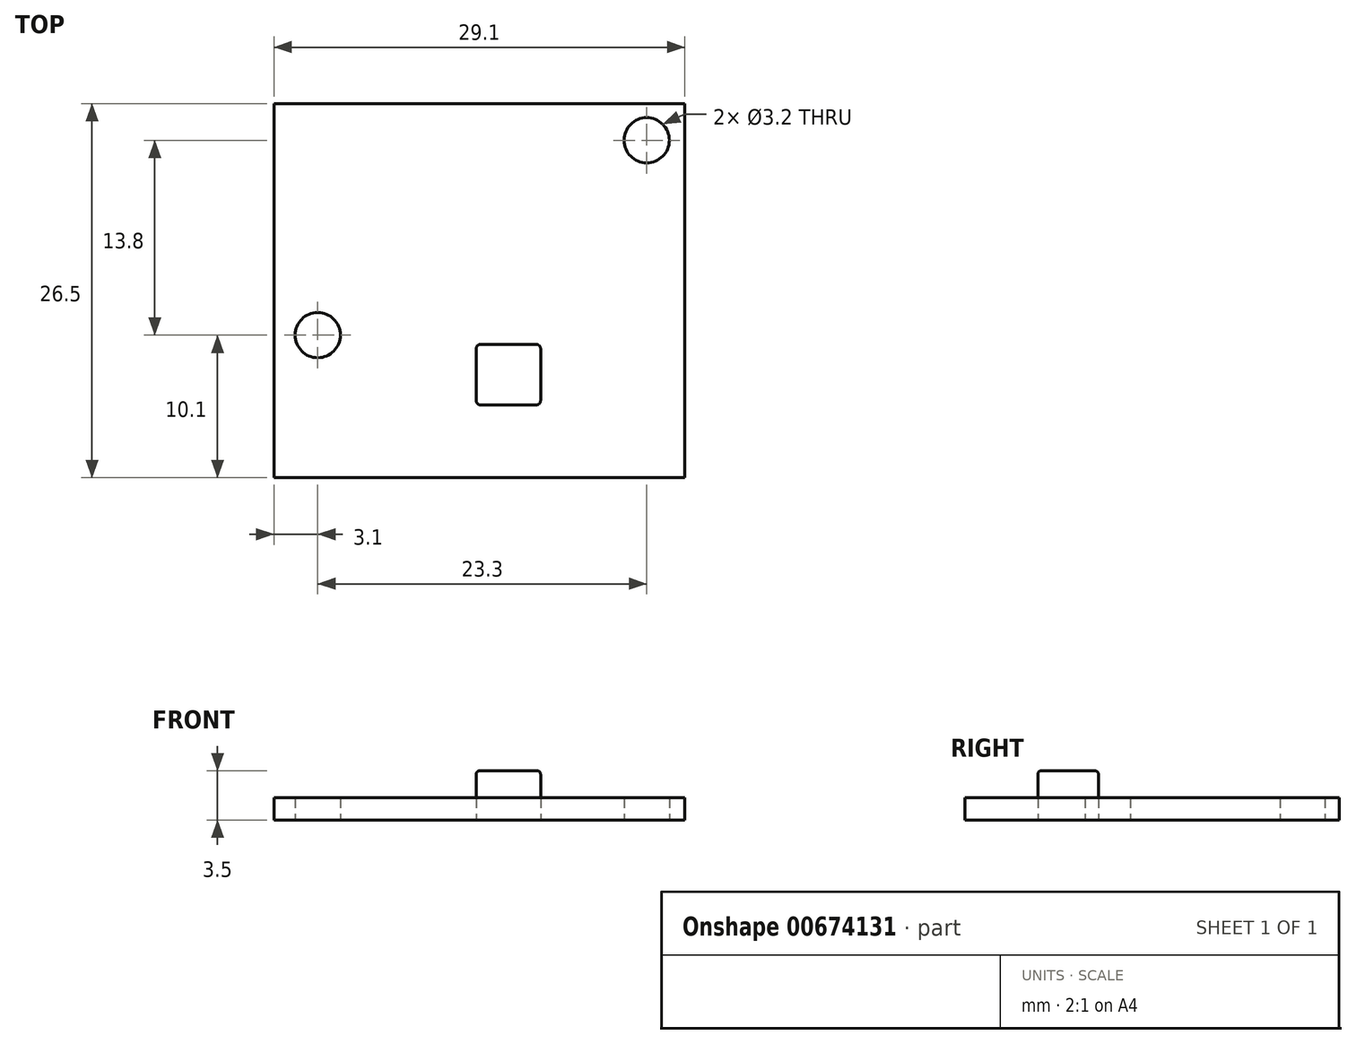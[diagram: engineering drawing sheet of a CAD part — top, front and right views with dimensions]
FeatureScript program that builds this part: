
annotation { "Feature Type Name" : "Feature", "Feature Type Description" : "" }
export const myFeature = defineFeature(function(context is Context, id is Id, definition is map)
    precondition{}
    {
        {
            var Q0;
            Q0=qCreatedBy(makeId("Top.planeOp"),FACE);
            var sketch = newSketch(context, id + "F0", { "sketchPlane" : qUnion([Q0])});
            skLineSegment(sketch, "E0.bottom", {"start": v(14.55, 13.25) * mm, "end": v(-14.55, 13.25) * mm});
            skLineSegment(sketch, "E0.top", {"start": v(14.55, -13.25) * mm, "end": v(-14.55, -13.25) * mm});
            skLineSegment(sketch, "E0.left", {"start": v(14.55, 13.25) * mm, "end": v(14.55, -13.25) * mm});
            skLineSegment(sketch, "E0.right", {"start": v(-14.55, 13.25) * mm, "end": v(-14.55, -13.25) * mm});
            skPoint(sketch, "E0.middle", {"position": v(0, 0) * mm});
            skCircle(sketch, "E1", {"center": v(-11.45, -3.15) * mm, "radius": 1.6 * mm});
            skCircle(sketch, "E2", {"center": v(11.85, 10.65) * mm, "radius": 1.6 * mm});
            skLineSegment(sketch, "E3.bottom", {"start": v(4.03, -8.1) * mm, "end": v(0.07, -8.1) * mm});
            skLineSegment(sketch, "E3.top", {"start": v(4.03, -3.8) * mm, "end": v(0.07, -3.8) * mm});
            skLineSegment(sketch, "E3.left", {"start": v(4.33, -7.8) * mm, "end": v(4.33, -4.1) * mm});
            skLineSegment(sketch, "E3.right", {"start": v(-0.23, -7.8) * mm, "end": v(-0.23, -4.1) * mm});
            skPoint(sketch, "E3.middle", {"position": v(2.05, -5.95) * mm});
            skPoint(sketch, "E4.visualSharp", {"position": v(-0.23, -3.8) * mm});
            skArc(sketch, "E4.filletArc", {"start": v(0.07, -3.8) * mm, "mid": v(-0.14, -3.9) * mm, "end": v(-0.23, -4.1) * mm});
            skPoint(sketch, "E5.visualSharp", {"position": v(4.33, -3.8) * mm});
            skArc(sketch, "E5.filletArc", {"start": v(4.33, -4.1) * mm, "mid": v(4.24, -3.9) * mm, "end": v(4.03, -3.8) * mm});
            skPoint(sketch, "E6.visualSharp", {"position": v(4.33, -8.1) * mm});
            skArc(sketch, "E6.filletArc", {"start": v(4.03, -8.1) * mm, "mid": v(4.24, -8) * mm, "end": v(4.33, -7.8) * mm});
            skPoint(sketch, "E7.visualSharp", {"position": v(-0.23, -8.1) * mm});
            skArc(sketch, "E7.filletArc", {"start": v(-0.23, -7.8) * mm, "mid": v(-0.14, -8) * mm, "end": v(0.07, -8.1) * mm});
            skSolve(sketch);
        }
        {
            var Q0;
            Q0=makeQuery(id+"F0.imprint","IMPRINT",FACE,{"disambiguationData":[TD([[makeQuery(id+"F0.imprint","IMPRINT",EDGE,{"derivedFrom":sQuery(id+"F0.wireOp",EDGE,"E0.bottom")}),1.0]])]});
            var Q1;
            Q1=makeQuery(id+"F0.imprint","IMPRINT",FACE,{"disambiguationData":[TD([[makeQuery(id+"F0.imprint","IMPRINT",EDGE,{"derivedFrom":sQuery(id+"F0.wireOp",EDGE,"E3.bottom")}),-1.0]])]});
            extrude(context, id + "F1", {"entities" : qUnion([Q0, Q1]), "depth" : 1.6 * mm, "offsetDistance" : 25 * mm});
        }
        {
            var Q0;
            Q0=makeQuery(id+"F0.imprint","IMPRINT",FACE,{"disambiguationData":[TD([[makeQuery(id+"F0.imprint","IMPRINT",EDGE,{"derivedFrom":sQuery(id+"F0.wireOp",EDGE,"E3.bottom")}),-1.0]])]});
            extrude(context, id + "F2", {"entities" : qUnion([Q0]), "depth" : 3.5 * mm, "offsetDistance" : 25 * mm});
        }
        {
            var Q0;
            Q0=makeQuery(id+"F2.opExtrude","CAP_FACE",FACE,{"disambiguationData":[OSD([sQuery(id+"F0.wireOp",EDGE,"E3.bottom"),sQuery(id+"F0.wireOp",EDGE,"E3.top"),sQuery(id+"F0.wireOp",EDGE,"E3.left"),sQuery(id+"F0.wireOp",EDGE,"E3.right")])],"isStart":false});
            fillet(context, id + "F3", {"entities" : qUnion([Q0]), "radius" : .25 * mm, "tangentPropagation" : true, "allowEdgeOverflow" : false});
        }
    });
